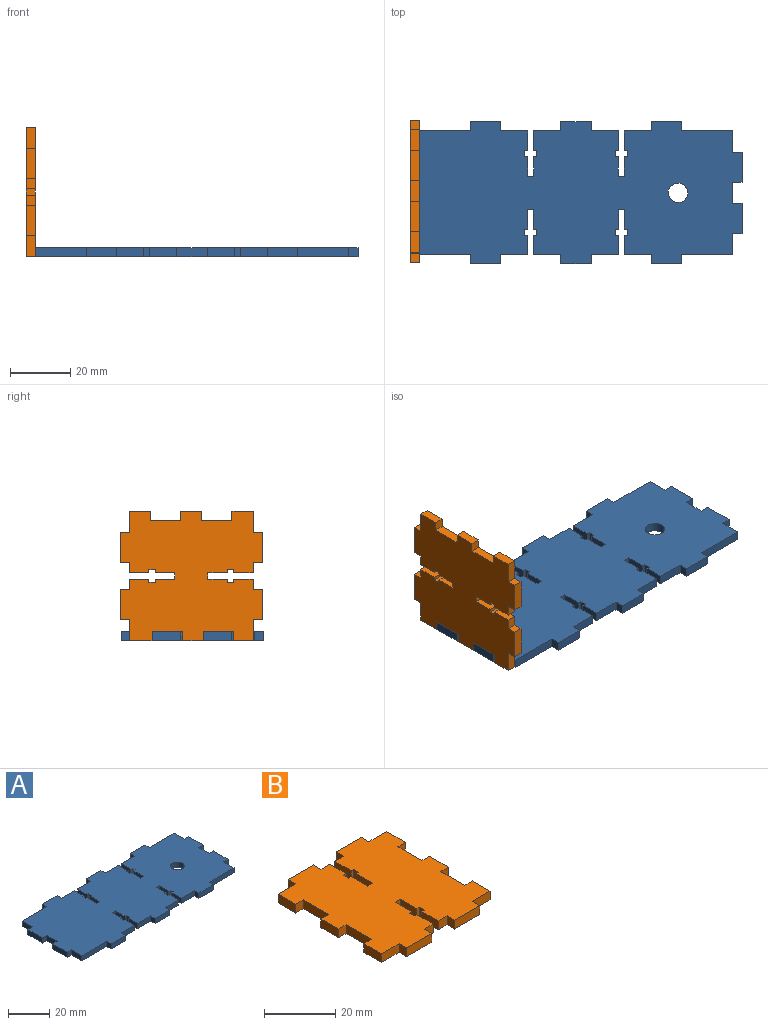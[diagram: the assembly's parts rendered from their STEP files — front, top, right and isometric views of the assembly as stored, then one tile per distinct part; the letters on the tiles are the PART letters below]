
ASSEMBLY  parts=2 mates=1
PART A: 95 faces, bbox 110x47x3 mm
  f0: plane 3x3mm, normal (0,-1,0), area 9mm2, adj f1,f92,f93,f94
  f1: plane 10x3mm, normal (1,0,0), area 30mm2, adj f0,f2,f93,f94
  f2: plane 3x3mm, normal (0,1,0), area 9mm2, adj f1,f3,f93,f94
  f3: plane 7x3mm, normal (1,0,0), area 21mm2, adj f2,f4,f93,f94
  f4: plane 3x3mm, normal (0,-1,0), area 9mm2, adj f3,f5,f93,f94
  f5: plane 10x3mm, normal (1,0,0), area 30mm2, adj f4,f6,f93,f94
  f6: plane 3x3mm, normal (0,1,0), area 9mm2, adj f5,f7,f93,f94
  f7: plane 7x3mm, normal (1,0,0), area 21mm2, adj f6,f8,f93,f94
  f8: plane 17x3mm, normal (0,1,0), area 51mm2, adj f7,f9,f93,f94
  f9: plane 3x3mm, normal (1,0,0), area 9mm2, adj f8,f10,f93,f94
  f10: plane 10x3mm, normal (0,1,0), area 30mm2, adj f9,f11,f93,f94
  f11: plane 3x3mm, normal (-1,0,0), area 9mm2, adj f10,f12,f93,f94
  f12: plane 9x3mm, normal (0,1,0), area 27mm2, adj f11,f13,f93,f94
  f13: plane 6.5x3mm, normal (-1,0,0), area 19.5mm2, adj f12,f14,f93,f94
  f14: plane 3x1mm, normal (0,-1,0), area 3mm2, adj f13,f15,f93,f94
  f15: plane 3x2mm, normal (-1,0,0), area 6mm2, adj f14,f16,f93,f94
  f16: plane 3x1mm, normal (0,1,0), area 3mm2, adj f15,f17,f93,f94
  f17: plane 6.5x3mm, normal (-1,0,0), area 19.5mm2, adj f16,f18,f93,f94
  f18: plane 3x2mm, normal (0,1,0), area 6mm2, adj f17,f19,f93,f94
  f19: plane 6.5x3mm, normal (1,0,0), area 19.5mm2, adj f18,f20,f93,f94
  f20: plane 3x1mm, normal (0,1,0), area 3mm2, adj f19,f21,f93,f94
  f21: plane 3x2mm, normal (1,0,0), area 6mm2, adj f20,f22,f93,f94
  f22: plane 3x1mm, normal (0,-1,0), area 3mm2, adj f21,f23,f93,f94
  f23: plane 6.5x3mm, normal (1,0,0), area 19.5mm2, adj f22,f24,f93,f94
  f24: plane 9x3mm, normal (0,1,0), area 27mm2, adj f23,f25,f93,f94
  f25: plane 3x3mm, normal (1,0,0), area 9mm2, adj f24,f26,f93,f94
  f26: plane 10x3mm, normal (0,1,0), area 30mm2, adj f25,f27,f93,f94
  f27: plane 3x3mm, normal (-1,0,0), area 9mm2, adj f26,f28,f93,f94
  f28: plane 9x3mm, normal (0,1,0), area 27mm2, adj f27,f29,f93,f94
  f29: plane 6.5x3mm, normal (-1,0,0), area 19.5mm2, adj f28,f30,f93,f94
  f30: plane 3x1mm, normal (0,-1,0), area 3mm2, adj f29,f31,f93,f94
  f31: plane 3x2mm, normal (-1,0,0), area 6mm2, adj f30,f32,f93,f94
  f32: plane 3x1mm, normal (0,1,0), area 3mm2, adj f31,f33,f93,f94
  f33: plane 6.5x3mm, normal (-1,0,0), area 19.5mm2, adj f32,f34,f93,f94
  f34: plane 3x2mm, normal (0,1,0), area 6mm2, adj f33,f35,f93,f94
  f35: plane 6.5x3mm, normal (1,0,0), area 19.5mm2, adj f34,f36,f93,f94
  f36: plane 3x1mm, normal (0,1,0), area 3mm2, adj f35,f37,f93,f94
  f37: plane 3x2mm, normal (1,0,0), area 6mm2, adj f36,f38,f93,f94
  f38: plane 3x1mm, normal (0,-1,0), area 3mm2, adj f37,f39,f93,f94
  f39: plane 6.5x3mm, normal (1,0,0), area 19.5mm2, adj f38,f40,f93,f94
  f40: plane 9x3mm, normal (0,1,0), area 27mm2, adj f39,f41,f93,f94
  f41: plane 3x3mm, normal (1,0,0), area 9mm2, adj f40,f42,f93,f94
  f42: plane 10x3mm, normal (0,1,0), area 30mm2, adj f41,f43,f93,f94
  f43: plane 3x3mm, normal (-1,0,0), area 9mm2, adj f42,f44,f93,f94
  f44: plane 17x3mm, normal (0,1,0), area 51mm2, adj f43,f45,f93,f94
  f45: plane 7x3mm, normal (-1,0,0), area 21mm2, adj f44,f46,f93,f94
  f46: plane 3x3mm, normal (0,1,0), area 9mm2, adj f45,f47,f93,f94
  f47: plane 10x3mm, normal (-1,0,0), area 30mm2, adj f46,f48,f93,f94
  f48: plane 3x3mm, normal (0,-1,0), area 9mm2, adj f47,f49,f93,f94
  f49: plane 7x3mm, normal (-1,0,0), area 21mm2, adj f48,f50,f93,f94
  f50: plane 3x3mm, normal (0,1,0), area 9mm2, adj f49,f51,f93,f94
  f51: plane 10x3mm, normal (-1,0,0), area 30mm2, adj f50,f52,f93,f94
  f52: plane 3x3mm, normal (0,-1,0), area 9mm2, adj f51,f53,f93,f94
  f53: plane 7x3mm, normal (-1,0,0), area 21mm2, adj f52,f54,f93,f94
  f54: plane 17x3mm, normal (0,-1,0), area 51mm2, adj f53,f55,f93,f94
  f55: plane 3x3mm, normal (-1,0,0), area 9mm2, adj f54,f56,f93,f94
  f56: plane 10x3mm, normal (0,-1,0), area 30mm2, adj f55,f57,f93,f94
  f57: plane 3x3mm, normal (1,0,0), area 9mm2, adj f56,f58,f93,f94
  f58: plane 9x3mm, normal (0,-1,0), area 27mm2, adj f57,f59,f93,f94
  f59: plane 6.5x3mm, normal (1,0,0), area 19.5mm2, adj f58,f60,f93,f94
  f60: plane 3x1mm, normal (0,1,0), area 3mm2, adj f59,f61,f93,f94
  f61: plane 3x2mm, normal (1,0,0), area 6mm2, adj f60,f62,f93,f94
  f62: plane 3x1mm, normal (0,-1,0), area 3mm2, adj f61,f63,f93,f94
  f63: plane 6.5x3mm, normal (1,0,0), area 19.5mm2, adj f62,f64,f93,f94
  f64: plane 3x2mm, normal (0,-1,0), area 6mm2, adj f63,f65,f93,f94
  f65: plane 6.5x3mm, normal (-1,0,0), area 19.5mm2, adj f64,f66,f93,f94
  f66: plane 3x1mm, normal (0,-1,0), area 3mm2, adj f65,f67,f93,f94
  f67: plane 3x2mm, normal (-1,0,0), area 6mm2, adj f66,f68,f93,f94
  f68: plane 3x1mm, normal (0,1,0), area 3mm2, adj f67,f69,f93,f94
  f69: plane 6.5x3mm, normal (-1,0,0), area 19.5mm2, adj f68,f70,f93,f94
  f70: plane 9x3mm, normal (0,-1,0), area 27mm2, adj f69,f71,f93,f94
  f71: plane 3x3mm, normal (-1,0,0), area 9mm2, adj f70,f72,f93,f94
  f72: plane 10x3mm, normal (0,-1,0), area 30mm2, adj f71,f73,f93,f94
  f73: plane 3x3mm, normal (1,0,0), area 9mm2, adj f72,f74,f93,f94
  f74: plane 9x3mm, normal (0,-1,0), area 27mm2, adj f73,f75,f93,f94
  f75: plane 6.5x3mm, normal (1,0,0), area 19.5mm2, adj f74,f76,f93,f94
  f76: plane 3x1mm, normal (0,1,0), area 3mm2, adj f75,f77,f93,f94
  f77: plane 3x2mm, normal (1,0,0), area 6mm2, adj f76,f78,f93,f94
  f78: plane 3x1mm, normal (0,-1,0), area 3mm2, adj f77,f79,f93,f94
  f79: plane 6.5x3mm, normal (1,0,0), area 19.5mm2, adj f78,f80,f93,f94
  f80: plane 3x2mm, normal (0,-1,0), area 6mm2, adj f79,f81,f93,f94
  f81: plane 6.5x3mm, normal (-1,0,0), area 19.5mm2, adj f80,f82,f93,f94
  f82: plane 3x1mm, normal (0,-1,0), area 3mm2, adj f81,f83,f93,f94
  f83: plane 3x2mm, normal (-1,0,0), area 6mm2, adj f82,f84,f93,f94
  f84: plane 3x1mm, normal (0,1,0), area 3mm2, adj f83,f85,f93,f94
  f85: plane 6.5x3mm, normal (-1,0,0), area 19.5mm2, adj f84,f86,f93,f94
  f86: plane 9x3mm, normal (0,-1,0), area 27mm2, adj f85,f87,f93,f94
  f87: plane 3x3mm, normal (-1,0,0), area 9mm2, adj f86,f88,f93,f94
  f88: plane 10x3mm, normal (0,-1,0), area 30mm2, adj f87,f89,f93,f94
  f89: plane 3x3mm, normal (1,0,0), area 9mm2, adj f88,f90,f93,f94
  f90: plane 17x3mm, normal (0,-1,0), area 51mm2, adj f89,f92,f93,f94
  f91: cylinder r=3.25mm len=6.5mm, axis (0,0,-1), area 61.3mm2, adj f93,f94
  f92: plane 7x3mm, normal (1,0,0), area 21mm2, adj f0,f90,f93,f94
  f93: plane 110x47mm, normal (0,0,1), area 4394.8mm2, adj f0,f1,f2,f3,f4,f5,f6,f7
  f94: plane 110x47mm, normal (0,0,-1), area 4394.8mm2, adj f0,f1,f2,f3,f4,f5,f6,f7
PART B: 62 faces, bbox 43x47x3 mm
  f0: plane 9.5x3mm, normal (1,0,0), area 28.5mm2, adj f1,f59,f60,f61
  f1: plane 3x3mm, normal (0,-1,0), area 9mm2, adj f0,f2,f60,f61
  f2: plane 7.5x3mm, normal (1,0,0), area 22.5mm2, adj f1,f3,f60,f61
  f3: plane 3x3mm, normal (0,1,0), area 9mm2, adj f2,f4,f60,f61
  f4: plane 9.5x3mm, normal (1,0,0), area 28.5mm2, adj f3,f5,f60,f61
  f5: plane 3x3mm, normal (0,-1,0), area 9mm2, adj f4,f6,f60,f61
  f6: plane 7.5x3mm, normal (1,0,0), area 22.5mm2, adj f5,f7,f60,f61
  f7: plane 7x3mm, normal (0,1,0), area 21mm2, adj f6,f8,f60,f61
  f8: plane 3x3mm, normal (1,0,0), area 9mm2, adj f7,f9,f60,f61
  f9: plane 10x3mm, normal (0,1,0), area 30mm2, adj f8,f10,f60,f61
  f10: plane 3x3mm, normal (-1,0,0), area 9mm2, adj f9,f11,f60,f61
  f11: plane 3.5x3mm, normal (0,1,0), area 10.5mm2, adj f10,f12,f60,f61
  f12: plane 6.5x3mm, normal (-1,0,0), area 19.5mm2, adj f11,f13,f60,f61
  f13: plane 3x1mm, normal (0,-1,0), area 3mm2, adj f12,f14,f60,f61
  f14: plane 3x2mm, normal (-1,0,0), area 6mm2, adj f13,f15,f60,f61
  f15: plane 3x1mm, normal (0,1,0), area 3mm2, adj f14,f16,f60,f61
  f16: plane 6.5x3mm, normal (-1,0,0), area 19.5mm2, adj f15,f17,f60,f61
  f17: plane 3x2mm, normal (0,1,0), area 6mm2, adj f16,f18,f60,f61
  f18: plane 6.5x3mm, normal (1,0,0), area 19.5mm2, adj f17,f19,f60,f61
  f19: plane 3x1mm, normal (0,1,0), area 3mm2, adj f18,f20,f60,f61
  f20: plane 3x2mm, normal (1,0,0), area 6mm2, adj f19,f21,f60,f61
  f21: plane 3x1mm, normal (0,-1,0), area 3mm2, adj f20,f22,f60,f61
  f22: plane 6.5x3mm, normal (1,0,0), area 19.5mm2, adj f21,f23,f60,f61
  f23: plane 3.5x3mm, normal (0,1,0), area 10.5mm2, adj f22,f24,f60,f61
  f24: plane 3x3mm, normal (1,0,0), area 9mm2, adj f23,f25,f60,f61
  f25: plane 10x3mm, normal (0,1,0), area 30mm2, adj f24,f26,f60,f61
  f26: plane 3x3mm, normal (-1,0,0), area 9mm2, adj f25,f27,f60,f61
  f27: plane 7x3mm, normal (0,1,0), area 21mm2, adj f26,f28,f60,f61
  f28: plane 7x3mm, normal (-1,0,0), area 21mm2, adj f27,f29,f60,f61
  f29: plane 3x3mm, normal (0,-1,0), area 9mm2, adj f28,f30,f60,f61
  f30: plane 10x3mm, normal (-1,0,0), area 30mm2, adj f29,f31,f60,f61
  f31: plane 3x3mm, normal (0,1,0), area 9mm2, adj f30,f32,f60,f61
  f32: plane 7x3mm, normal (-1,0,0), area 21mm2, adj f31,f33,f60,f61
  f33: plane 3x3mm, normal (0,-1,0), area 9mm2, adj f32,f34,f60,f61
  f34: plane 10x3mm, normal (-1,0,0), area 30mm2, adj f33,f35,f60,f61
  f35: plane 3x3mm, normal (0,1,0), area 9mm2, adj f34,f36,f60,f61
  f36: plane 7x3mm, normal (-1,0,0), area 21mm2, adj f35,f37,f60,f61
  f37: plane 7x3mm, normal (0,-1,0), area 21mm2, adj f36,f38,f60,f61
  f38: plane 3x3mm, normal (-1,0,0), area 9mm2, adj f37,f39,f60,f61
  f39: plane 10x3mm, normal (0,-1,0), area 30mm2, adj f38,f40,f60,f61
  f40: plane 3x3mm, normal (1,0,0), area 9mm2, adj f39,f41,f60,f61
  f41: plane 3.5x3mm, normal (0,-1,0), area 10.5mm2, adj f40,f42,f60,f61
  f42: plane 6.5x3mm, normal (1,0,0), area 19.5mm2, adj f41,f43,f60,f61
  f43: plane 3x1mm, normal (0,1,0), area 3mm2, adj f42,f44,f60,f61
  f44: plane 3x2mm, normal (1,0,0), area 6mm2, adj f43,f45,f60,f61
  f45: plane 3x1mm, normal (0,-1,0), area 3mm2, adj f44,f46,f60,f61
  f46: plane 6.5x3mm, normal (1,0,0), area 19.5mm2, adj f45,f47,f60,f61
  f47: plane 3x2mm, normal (0,-1,0), area 6mm2, adj f46,f48,f60,f61
  f48: plane 6.5x3mm, normal (-1,0,0), area 19.5mm2, adj f47,f49,f60,f61
  f49: plane 3x1mm, normal (0,-1,0), area 3mm2, adj f48,f50,f60,f61
  f50: plane 3x2mm, normal (-1,0,0), area 6mm2, adj f49,f51,f60,f61
  f51: plane 3x1mm, normal (0,1,0), area 3mm2, adj f50,f52,f60,f61
  f52: plane 6.5x3mm, normal (-1,0,0), area 19.5mm2, adj f51,f53,f60,f61
  f53: plane 3.5x3mm, normal (0,-1,0), area 10.5mm2, adj f52,f54,f60,f61
  f54: plane 3x3mm, normal (-1,0,0), area 9mm2, adj f53,f55,f60,f61
  f55: plane 10x3mm, normal (0,-1,0), area 30mm2, adj f54,f56,f60,f61
  f56: plane 3x3mm, normal (1,0,0), area 9mm2, adj f55,f57,f60,f61
  f57: plane 7x3mm, normal (0,-1,0), area 21mm2, adj f56,f58,f60,f61
  f58: plane 7x3mm, normal (1,0,0), area 21mm2, adj f57,f59,f60,f61
  f59: plane 3x3mm, normal (0,1,0), area 9mm2, adj f0,f58,f60,f61
  f60: plane 47x43mm, normal (0,0,1), area 1698mm2, adj f0,f1,f2,f3,f4,f5,f6,f7
  f61: plane 47x43mm, normal (0,0,-1), area 1698mm2, adj f0,f1,f2,f3,f4,f5,f6,f7
PLACE A t=(-4.21,7.58,-0.77)mm
PLACE B rot(axis=(0,1,0),90deg) t=(-7.21,5.08,35.23)mm
MATE fastened B.f5 <-> A.f46  axis (0,-1,0) through (-5.71,41.58,0.73)mm
